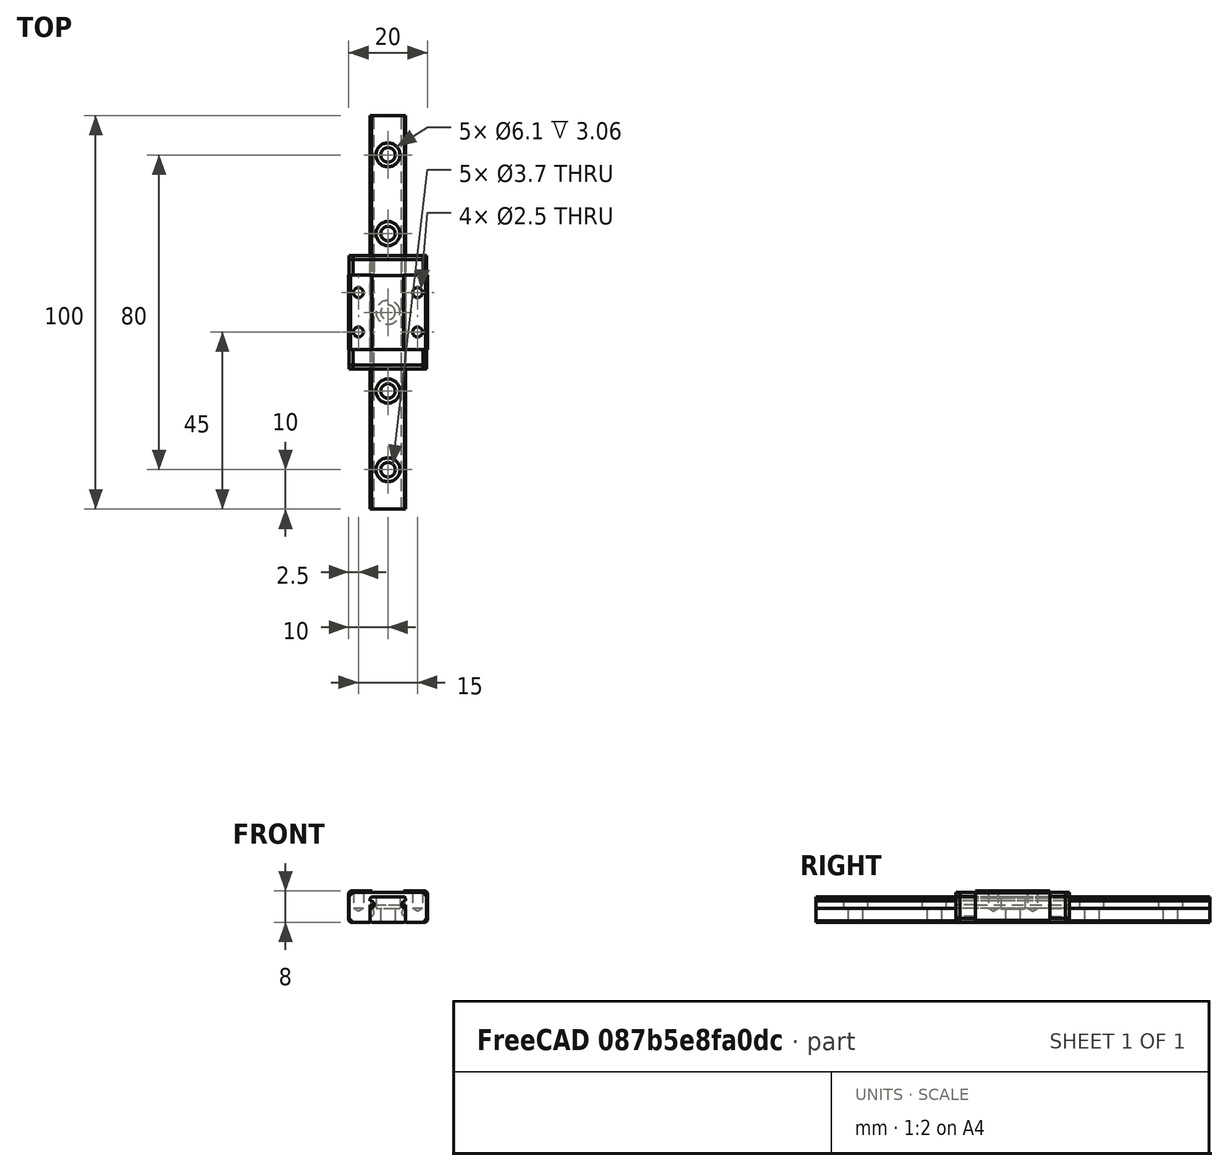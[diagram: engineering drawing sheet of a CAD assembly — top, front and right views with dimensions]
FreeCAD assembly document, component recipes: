
FREECAD ASSEMBLY — COMPONENT RECIPES ("MGN9")

This assembly document has 2 components, labeled P0..P1 below (a component is one placed body or linked part). 2 of them carry a construction recipe — the FreeCAD feature program that regenerates the part from scratch, quoted from this document or its linked companion documents; the rest are supplied as boundary geometry only. No exploded tour is included for this assembly.
COMPONENT P0 — recipe-attached ("Rail", modeled in this document).
Construction recipe (the document's own serialized feature program — sketch geometry with constraints, then the solid features built on it; lengths are millimeters unless a unit is written):

FEATURE [Sketcher::SketchObject] Sketch
  FullyConstrained = true
  MapMode = 5
  Placement = pos=(0,0,0) rot=(1,0,0;1.5708rad)
  Support = -> [XZ_Plane001]
  sketch-geometry (8):
    g0: LineSegment StartX=-4.5 StartY=6.5 StartZ=0 EndX=4.5 EndY=6.5 EndZ=0
    g1: LineSegment StartX=4.5 StartY=6.5 StartZ=0 EndX=4.5 EndY=5.5 EndZ=0
    g2: LineSegment StartX=4.5 StartY=0 StartZ=0 EndX=-4.5 EndY=0 EndZ=0
    g3: LineSegment StartX=-4.5 StartY=0 StartZ=0 EndX=-4.5 EndY=3.5 EndZ=0
    g4: ArcOfCircle CenterX=-4.5 CenterY=4.5 CenterZ=0 NormalX=0 NormalY=0 NormalZ=1 AngleXU=0 Radius=1 StartAngle=4.71239 EndAngle=7.85398
    g5: LineSegment StartX=-4.5 StartY=5.5 StartZ=0 EndX=-4.5 EndY=6.5 EndZ=0
    g6: ArcOfCircle CenterX=4.5 CenterY=4.5 CenterZ=0 NormalX=0 NormalY=0 NormalZ=1 AngleXU=0 Radius=1 StartAngle=1.5708 EndAngle=4.71239
    g7: LineSegment StartX=4.5 StartY=3.5 StartZ=0 EndX=4.5 EndY=0 EndZ=0
  constraints (22):
    c: Coincident(g0,g1)
    c: Coincident(g7,g2)
    c: Coincident(g2,g3)
    c: Coincident(g5,g0)
    c: Symmetric(g2,g7,g-2)
    c: Symmetric(g0,g0,g-2)
    c: Vertical(g3)
    c: DistanceX(g2,g2) = 9
    c: DistanceY(g3,g5) = 6.5
    c: PointOnObject(g2,g-1)
    c: PointOnObject(g4,g3)
    c: DistanceY(g-1,g4) = 4.5
    c: Radius(g4) = 1
    c: Coincident(g3,g4)
    c: Coincident(g5,g4)
    c: Vertical(g5)
    c: Vertical(g4,g3)
    c: PointOnObject(g6,g1)
    c: Coincident(g1,g6)
    c: Coincident(g7,g6)
    c: Symmetric(g4,g6,g-2)
    c: Symmetric(g3,g6,g-2)
FEATURE [PartDesign::Pad] Pad
  Direction = (0,-1,-2e-16)
  Length = 100
  Length2 = 10
  Midplane = true
  Placement = pos=(0,0,0) rot=(1,0,0;1.5708rad)
  Profile = -> Sketch
  ReferenceAxis = -> Sketch [N_Axis]
  Type = 0
  expr: Length = <<Variables>>.Length
FEATURE [PartDesign::Chamfer] Chamfer003
  Angle = 45
  Base = -> Pad [Edge2,Edge11,Edge14,Edge1]
  BaseFeature = -> Pad
  ChamferType = 0
  FlipDirection = false
  Placement = pos=(0,0,0) rot=(1,0,0;1.5708rad)
  Size = 0.35
  Size2 = 1
  SupportTransform = false
  UseAllEdges = false
FEATURE [Sketcher::SketchObject] Sketch004
  AttachmentOffset = pos=(0,0,-6.5) rot=(0,0,1;0rad)
  FullyConstrained = true
  MapMode = 3
  Placement = pos=(-7e-16,7e-16,6.5) rot=(0.707107,0.707107,0;3.14159rad)
  Support = -> [Y_Axis001]
  sketch-geometry (19):
    g0: Circle CenterX=0 CenterY=0 CenterZ=0 NormalX=0 NormalY=0 NormalZ=1 AngleXU=0 Radius=1.5
    g1: Circle CenterX=-20 CenterY=0 CenterZ=0 NormalX=0 NormalY=0 NormalZ=1 AngleXU=0 Radius=1.5
    g2: Circle CenterX=-40 CenterY=0 CenterZ=0 NormalX=0 NormalY=0 NormalZ=1 AngleXU=0 Radius=1.5
    g3: Circle CenterX=-60 CenterY=0 CenterZ=0 NormalX=0 NormalY=0 NormalZ=1 AngleXU=0 Radius=1.5
    g4: Circle CenterX=-80 CenterY=0 CenterZ=0 NormalX=0 NormalY=0 NormalZ=1 AngleXU=0 Radius=1.5
    g5: Circle CenterX=-100 CenterY=0 CenterZ=0 NormalX=0 NormalY=0 NormalZ=1 AngleXU=0 Radius=1.5
    g6: Circle CenterX=-120 CenterY=0 CenterZ=0 NormalX=0 NormalY=0 NormalZ=1 AngleXU=0 Radius=1.5
    g7: Circle CenterX=-140 CenterY=0 CenterZ=0 NormalX=0 NormalY=0 NormalZ=1 AngleXU=0 Radius=1.5
    g8: Circle CenterX=-160 CenterY=0 CenterZ=0 NormalX=0 NormalY=0 NormalZ=1 AngleXU=0 Radius=1.5
    g9: Circle CenterX=-180 CenterY=0 CenterZ=0 NormalX=0 NormalY=0 NormalZ=1 AngleXU=0 Radius=1.5
    g10: Circle CenterX=20 CenterY=0 CenterZ=0 NormalX=0 NormalY=0 NormalZ=1 AngleXU=0 Radius=1.5
    g11: Circle CenterX=40 CenterY=0 CenterZ=0 NormalX=0 NormalY=0 NormalZ=1 AngleXU=0 Radius=1.5
    g12: Circle CenterX=60 CenterY=0 CenterZ=0 NormalX=0 NormalY=0 NormalZ=1 AngleXU=0 Radius=1.5
    g13: Circle CenterX=80 CenterY=0 CenterZ=0 NormalX=0 NormalY=0 NormalZ=1 AngleXU=0 Radius=1.5
    g14: Circle CenterX=100 CenterY=0 CenterZ=0 NormalX=0 NormalY=0 NormalZ=1 AngleXU=0 Radius=1.5
    g15: Circle CenterX=120 CenterY=0 CenterZ=0 NormalX=0 NormalY=0 NormalZ=1 AngleXU=0 Radius=1.5
    g16: Circle CenterX=140 CenterY=0 CenterZ=0 NormalX=0 NormalY=0 NormalZ=1 AngleXU=0 Radius=1.5
    g17: Circle CenterX=160 CenterY=0 CenterZ=0 NormalX=0 NormalY=0 NormalZ=1 AngleXU=0 Radius=1.5
    g18: Circle CenterX=180 CenterY=0 CenterZ=0 NormalX=0 NormalY=0 NormalZ=1 AngleXU=0 Radius=1.5
  constraints (30):
    c: PointOnObject(g1,g-1)
    c: PointOnObject(g2,g-1)
    c: PointOnObject(g3,g-1)
    c: PointOnObject(g4,g-1)
    c: PointOnObject(g5,g-1)
    c: PointOnObject(g6,g-1)
    c: PointOnObject(g7,g-1)
    c: PointOnObject(g8,g-1)
    c: PointOnObject(g9,g-1)
    c: Equal(g0, g1-g18) x18
    c: Diameter(g0) = 3
    c: Symmetric(g9,g18,g-2)
    c: Symmetric(g8,g17,g-2)
    c: DistanceX(g9,g8) = 20
    c: Symmetric(g7,g16,g-2)
    c: DistanceX(g8,g7) = 20
    c: Symmetric(g6,g15,g-2)
    c: DistanceX(g7,g6) = 20
    c: Symmetric(g14,g5,g-2)
    c: DistanceX(g6,g5) = 20
    c: Symmetric(g4,g13,g-2)
    c: DistanceX(g5,g4) = 20
    c: Symmetric(g12,g3,g-2)
    c: DistanceX(g4,g3) = 20
    c: Symmetric(g11,g2,g-2)
    c: DistanceX(g3,g2) = 20
    c: Symmetric(g10,g1,g-2)
    c: DistanceX(g2,g1) = 20
    c: DistanceX(g1,g0) = 20
    c: Coincident(g0,g-1)
FEATURE [PartDesign::Hole] Hole001
  BaseFeature = -> Chamfer003
  CustomThreadClearance = 0
  Depth = 733.603
  DepthType = 1
  Diameter = 3.7
  DrillForDepth = false
  DrillPoint = 1
  DrillPointAngle = 118
  HoleCutCountersinkAngle = 90
  HoleCutCustomValues = false
  HoleCutDepth = 3.06
  HoleCutDiameter = 6.1
  HoleCutType = 1
  ModelThread = false
  Placement = pos=(0,0,0) rot=(1,0,0;1.5708rad)
  Profile = -> Sketch004
  Reversed = true
  Tapered = false
  TaperedAngle = 90
  ThreadClass = 0
  ThreadDepth = 733.603
  ThreadDepthType = 0
  ThreadDirection = 0
  ThreadFit = 0
  ThreadSize = 0
  ThreadType = 0
  Threaded = false
  UseCustomThreadClearance = false
FEATURE [PartDesign::Body] Body  label="RailBody"
  Group = -> [Sketch,Pad,Sketch004,Chamfer003,Hole001]
  Origin = -> Origin001
  Tip = -> Hole001
COMPONENT P1 — recipe-attached ("Unit", modeled in this document).
Construction recipe (the document's own serialized feature program — sketch geometry with constraints, then the solid features built on it; lengths are millimeters unless a unit is written):

FEATURE [PartDesign::ShapeBinder] ShapeBinder
  Placement = pos=(0,0,0) rot=(1,0,0;1.5708rad)
  Support = -> [Sketch001]
  TraceSupport = false
FEATURE [PartDesign::Pad] Pad001
  Direction = (0,1,2e-16)
  Length = 18.9
  Length2 = 10
  Midplane = true
  Placement = pos=(0,0,0) rot=(1,0,0;1.5708rad)
  Profile = -> ShapeBinder
  Type = 0
FEATURE [PartDesign::ShapeBinder] ShapeBinder001
  Placement = pos=(0,0,0) rot=(1,0,0;1.5708rad)
  Support = -> [Sketch002]
  TraceSupport = false
FEATURE [PartDesign::Pad] Pad002
  Direction = (0,1,2e-16)
  Length = 4
  Length2 = 10
  Placement = pos=(0,0,0) rot=(1,0,0;1.5708rad)
  Profile = -> ShapeBinder001
  Type = 0
FEATURE [PartDesign::ShapeBinder] ShapeBinder002
  Placement = pos=(0,0,0) rot=(1,0,0;1.5708rad)
  Support = -> [Sketch002]
  TraceSupport = false
FEATURE [PartDesign::Pad] Pad003
  Direction = (0,1,2e-16)
  Length = 4
  Length2 = 10
  Placement = pos=(0,0,0) rot=(1,0,0;1.5708rad)
  Profile = -> ShapeBinder002
  Reversed = true
  Type = 0
FEATURE [PartDesign::Chamfer] Chamfer
  Angle = 45
  Base = -> Pad003 [Edge5,Edge8,Edge11,Edge2]
  BaseFeature = -> Pad003
  ChamferType = 0
  FlipDirection = false
  Placement = pos=(0,0,0) rot=(1,0,0;1.5708rad)
  Size = 1
  Size2 = 1
  SupportTransform = false
  UseAllEdges = false
FEATURE [PartDesign::Chamfer] Chamfer001
  Angle = 45
  Base = -> Pad001 [Edge5,Edge20,Edge23,Edge2]
  BaseFeature = -> Pad001
  ChamferType = 0
  FlipDirection = false
  Placement = pos=(0,0,0) rot=(1,0,0;1.5708rad)
  Size = 0.5
  Size2 = 1
  SupportTransform = false
  UseAllEdges = false
FEATURE [PartDesign::Chamfer] Chamfer002
  Angle = 45
  Base = -> Pad002 [Edge8,Edge5,Edge2,Edge11]
  BaseFeature = -> Pad002
  ChamferType = 0
  FlipDirection = false
  Placement = pos=(0,0,0) rot=(1,0,0;1.5708rad)
  Size = 1
  Size2 = 1
  SupportTransform = false
  UseAllEdges = false
FEATURE [PartDesign::Body] Body002  label="Returner001"
  Group = -> [ShapeBinder001,Pad002,Chamfer002]
  Origin = -> Origin004
  Placement = pos=(0,9.4,0) rot=(0,0,1;0rad)
  Tip = -> Chamfer002
FEATURE [PartDesign::ShapeBinder] ShapeBinder003
  Placement = pos=(0,0,0) rot=(1,0,0;1.5708rad)
  Support = -> [Sketch002]
  TraceSupport = false
FEATURE [PartDesign::Pad] Pad004
  Direction = (0,1,2e-16)
  Length = 1
  Length2 = 10
  Placement = pos=(0,0,0) rot=(1,0,0;1.5708rad)
  Profile = -> ShapeBinder003
  Type = 0
FEATURE [PartDesign::Chamfer] Chamfer004
  Angle = 45
  Base = -> Pad004 [Edge8,Edge5,Edge11,Edge2]
  BaseFeature = -> Pad004
  ChamferType = 0
  FlipDirection = false
  Placement = pos=(0,0,0) rot=(1,0,0;1.5708rad)
  Size = 1
  Size2 = 1
  SupportTransform = false
  UseAllEdges = false
FEATURE [PartDesign::Body] Body004  label="wiper001"
  Group = -> [ShapeBinder003,Pad004,Chamfer004]
  Origin = -> Origin006
  Placement = pos=(0,13.4,0) rot=(0,0,1;0rad)
  Tip = -> Chamfer004
FEATURE [PartDesign::ShapeBinder] ShapeBinder004
  Placement = pos=(0,0,0) rot=(1,0,0;1.5708rad)
  Support = -> [Sketch002]
  TraceSupport = false
FEATURE [PartDesign::Pad] Pad005
  Direction = (0,1,2e-16)
  Length = 1
  Length2 = 10
  Placement = pos=(0,0,0) rot=(1,0,0;1.5708rad)
  Profile = -> ShapeBinder004
  Reversed = true
  Type = 0
FEATURE [PartDesign::Chamfer] Chamfer005
  Angle = 45
  Base = -> Pad003 [Edge8,Edge11,Edge5,Edge2]
  BaseFeature = -> Pad003
  ChamferType = 0
  FlipDirection = false
  Placement = pos=(0,0,0) rot=(1,0,0;1.5708rad)
  Size = 1
  Size2 = 1
  SupportTransform = false
  UseAllEdges = false
FEATURE [PartDesign::Body] Body003  label="Returner002"
  Group = -> [ShapeBinder002,Pad003,Chamfer,Chamfer005]
  Origin = -> Origin005
  Placement = pos=(0,-9.4,0) rot=(0,0,1;0rad)
  Tip = -> Chamfer005
FEATURE [PartDesign::Chamfer] Chamfer006
  Angle = 45
  Base = -> Pad005 [Edge5,Edge2,Edge8,Edge11]
  BaseFeature = -> Pad005
  ChamferType = 0
  FlipDirection = false
  Placement = pos=(0,0,0) rot=(1,0,0;1.5708rad)
  Size = 1
  Size2 = 1
  SupportTransform = false
  UseAllEdges = false
FEATURE [PartDesign::Body] Body005  label="wiper002"
  Group = -> [ShapeBinder004,Pad005,Chamfer006]
  Origin = -> Origin007
  Placement = pos=(0,-13.4,0) rot=(0,0,1;0rad)
  Tip = -> Chamfer006
FEATURE [Sketcher::SketchObject] Sketch003
  FullyConstrained = true
  MapMode = 5
  Placement = pos=(0,1.8e-15,8) rot=(0,0,1;3.14159rad)
  Support = -> [Chamfer001]
  sketch-geometry (4):
    g0: Circle CenterX=-7.5 CenterY=5 CenterZ=0 NormalX=0 NormalY=0 NormalZ=1 AngleXU=0 Radius=1.5
    g1: Circle CenterX=7.5 CenterY=5 CenterZ=0 NormalX=0 NormalY=0 NormalZ=1 AngleXU=0 Radius=1.5
    g2: Circle CenterX=-7.5 CenterY=-5 CenterZ=0 NormalX=0 NormalY=0 NormalZ=1 AngleXU=0 Radius=1.5
    g3: Circle CenterX=7.5 CenterY=-5 CenterZ=0 NormalX=0 NormalY=0 NormalZ=1 AngleXU=0 Radius=1.5
  constraints (9):
    c: Symmetric(g0,g2,g-1)
    c: Symmetric(g0,g1,g-2)
    c: Symmetric(g2,g3,g-2)
    c: DistanceY(g2,g0) = 10
    c: DistanceX(g0,g1) = 15
    c: Equal(g0,g1)
    c: Equal(g0,g2)
    c: Equal(g0,g3)
    c: Diameter(g0) = 3
FEATURE [PartDesign::Hole] Hole
  BaseFeature = -> Chamfer001
  CustomThreadClearance = 0
  Depth = 4.4
  DepthType = 0
  Diameter = 2.5
  DrillForDepth = false
  DrillPoint = 1
  DrillPointAngle = 118
  HoleCutCountersinkAngle = 90
  HoleCutCustomValues = false
  HoleCutDepth = 0
  HoleCutDiameter = 6.1
  HoleCutType = 0
  ModelThread = false
  Placement = pos=(0,0,0) rot=(1,0,0;1.5708rad)
  Profile = -> Sketch003
  Tapered = false
  TaperedAngle = 90
  ThreadClass = 0
  ThreadDepth = 4.4
  ThreadDepthType = 0
  ThreadDirection = 0
  ThreadFit = 0
  ThreadSize = 9
  ThreadType = 1
  Threaded = true
  UseCustomThreadClearance = false
FEATURE [PartDesign::Body] Body001  label="UnitBody"
  Group = -> [ShapeBinder,Pad001,Chamfer001,Sketch003,Hole]
  Origin = -> Origin003
  Tip = -> Hole
PROVENANCE & LICENSES
A FreeCAD (.FCStd) document from a public repository crawl; recipes are the document's own serialized feature recipes (and, for linked parts, companion documents' recipes).
License: gpl-3.0.
